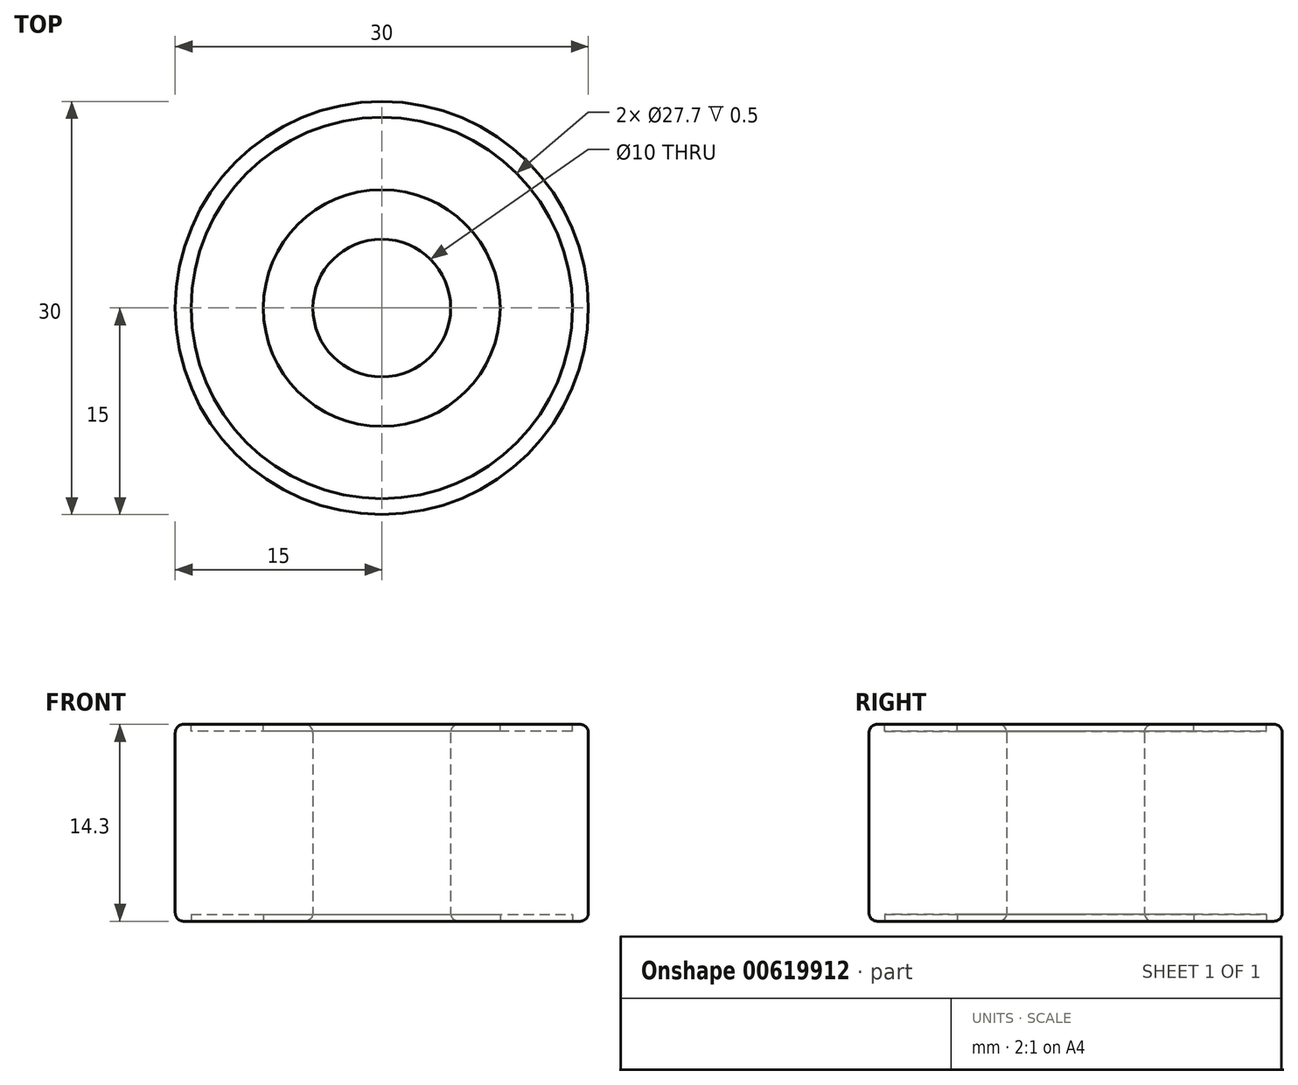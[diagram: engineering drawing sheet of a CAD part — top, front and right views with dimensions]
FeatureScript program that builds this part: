
annotation { "Feature Type Name" : "Feature", "Feature Type Description" : "" }
export const myFeature = defineFeature(function(context is Context, id is Id, definition is map)
    precondition{}
    {
        {
            var Q0;
            Q0=qCreatedBy(makeId("Top.planeOp"),FACE);
            var sketch = newSketch(context, id + "F0", { "sketchPlane" : qUnion([Q0])});
            skCircle(sketch, "E0", {"center": v(0, 0) * mm, "radius": 5 * mm});
            skCircle(sketch, "E1", {"center": v(0, 0) * mm, "radius": 15 * mm});
            skSolve(sketch);
        }
        {
            var Q0;
            Q0=qSketchRegion(id+"F0",true);
            extrude(context, id + "F1", {"entities" : qUnion([Q0]), "depth" : 14.3 * mm, "offsetDistance" : 25 * mm});
        }
        {
            var Q0;
            Q0=makeQuery(id+"F1.opExtrude","SWEPT_FACE",FACE,{"disambiguationData":[OSD([sQuery(id+"F0.wireOp",EDGE,"E0")])]});
            var Q1;
            Q1=makeQuery(id+"F1.opExtrude","SWEPT_FACE",FACE,{"disambiguationData":[OSD([sQuery(id+"F0.wireOp",EDGE,"E1")])]});
            fillet(context, id + "F2", {"entities" : qUnion([Q0, Q1]), "radius" : .6 * mm, "tangentPropagation" : true, "allowEdgeOverflow" : false});
        }
        {
            var Q0;
            Q0=makeQuery(id+"F1.opExtrude","CAP_FACE",FACE,{"disambiguationData":[OSD([sQuery(id+"F0.wireOp",EDGE,"E0"),sQuery(id+"F0.wireOp",EDGE,"E1")])],"isStart":false});
            var sketch = newSketch(context, id + "F3", { "sketchPlane" : qUnion([Q0])});
            skCircle(sketch, "E2", {"center": v(0, 0) * mm, "radius": 8.6 * mm});
            skCircle(sketch, "E3", {"center": v(0, 0) * mm, "radius": 13.85 * mm});
            skSolve(sketch);
        }
        {
            var Q0;
            Q0=qSketchRegion(id+"F3",true);
            extrude(context, id + "F4", {"entities" : qUnion([Q0]), "operationType" : NewBodyOperationType.REMOVE, "oppositeDirection" : true, "depth" : .5 * mm, "offsetDistance" : 25 * mm});
        }
        {
            var Q0;
            Q0=makeQuery(id+"F1.opExtrude","CAP_FACE",FACE,{"disambiguationData":[OSD([sQuery(id+"F0.wireOp",EDGE,"E0"),sQuery(id+"F0.wireOp",EDGE,"E1")])],"isStart":true});
            var sketch = newSketch(context, id + "F5", { "sketchPlane" : qUnion([Q0])});
            skCircle(sketch, "E4", {"center": v(0, 0) * mm, "radius": 8.6 * mm});
            skCircle(sketch, "E5", {"center": v(0, 0) * mm, "radius": 13.85 * mm});
            skSolve(sketch);
        }
        {
            var Q0;
            Q0=qSketchRegion(id+"F5",true);
            extrude(context, id + "F6", {"entities" : qUnion([Q0]), "operationType" : NewBodyOperationType.REMOVE, "oppositeDirection" : true, "depth" : .5 * mm, "offsetDistance" : 25 * mm});
        }
    });
